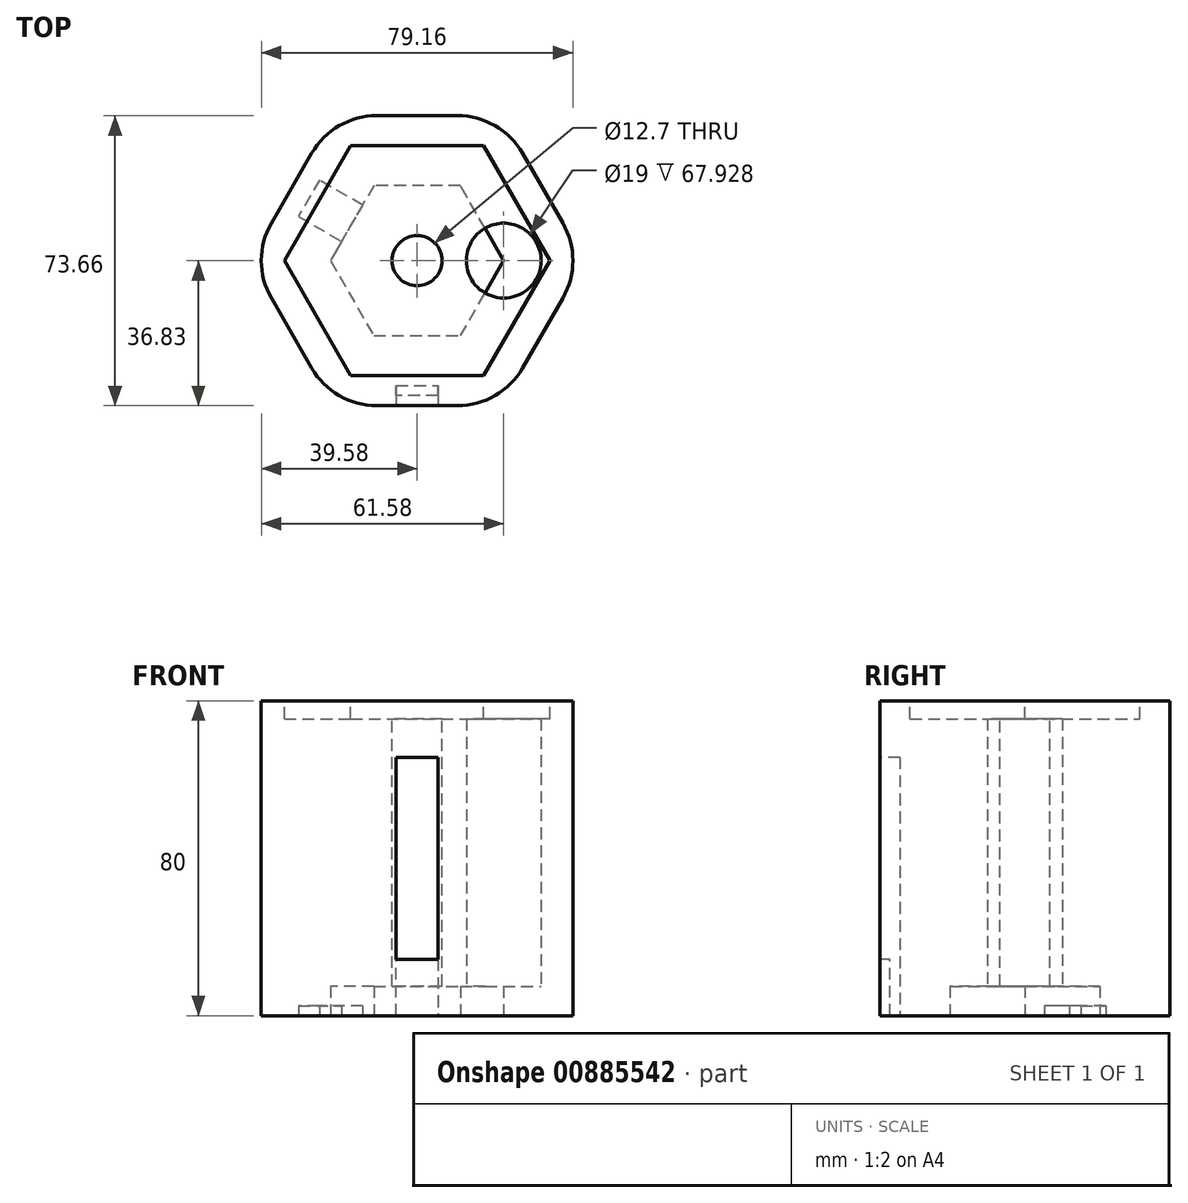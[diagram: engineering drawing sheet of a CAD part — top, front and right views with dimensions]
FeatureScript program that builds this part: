
annotation { "Feature Type Name" : "Feature", "Feature Type Description" : "" }
export const myFeature = defineFeature(function(context is Context, id is Id, definition is map)
    precondition{}
    {
        {
            var Q0;
            Q0=qCreatedBy(makeId("Front.planeOp"),FACE);
            var sketch = newSketch(context, id + "F0", { "sketchPlane" : qUnion([Q0])});
            skLineSegment(sketch, "E0", {"start": v(0, 111.03) * mm, "end": v(0, -71.9) * mm});
            skSolve(sketch);
        }
        {
            var Q0;
            Q0=qCreatedBy(makeId("Top.planeOp"),FACE);
            var sketch = newSketch(context, id + "F1", { "sketchPlane" : qUnion([Q0])});
            skCircle(sketch, "E1.cCircle", {"center": v(0, 0) * mm, "radius": 36.83 * mm, "construction": true});
            skLineSegment(sketch, "E1.0", {"start": v(-21.26, 36.83) * mm, "end": v(21.26, 36.83) * mm});
            skLineSegment(sketch, "E1.1", {"start": v(21.26, 36.83) * mm, "end": v(42.53, 0) * mm});
            skLineSegment(sketch, "E1.2", {"start": v(42.53, 0) * mm, "end": v(21.26, -36.83) * mm});
            skLineSegment(sketch, "E1.3", {"start": v(21.26, -36.83) * mm, "end": v(-21.26, -36.83) * mm});
            skLineSegment(sketch, "E1.4", {"start": v(-21.26, -36.83) * mm, "end": v(-42.53, 0) * mm});
            skLineSegment(sketch, "E1.5", {"start": v(-42.53, 0) * mm, "end": v(-21.26, 36.83) * mm});
            skPoint(sketch, "E1.0.midPoint", {"position": v(0, 36.83) * mm});
            skSolve(sketch);
        }
        {
            var Q0;
            Q0=makeQuery(id+"F1.imprint","IMPRINT",FACE,{"disambiguationData":[TD([[makeQuery(id+"F1.imprint","IMPRINT",EDGE,{"derivedFrom":sQuery(id+"F1.wireOp",EDGE,"E1.0")}),-1.0]])]});
            extrude(context, id + "F2", {"entities" : qUnion([Q0]), "depth" : 80 * mm, "offsetDistance" : 25.4 * mm});
        }
        {
            var Q0;
            Q0=qCreatedBy(makeId("Top.planeOp"),FACE);
            cPlane(context, id + "F3", {"entities" : qUnion([Q0]), "cplaneType" : CPlaneType.OFFSET, "offset" : 7.5 * mm, "width" : 152.4 * mm, "height" : 152.4 * mm});
        }
        {
            var Q0;
            Q0=qCreatedBy(id+"F3.planeOp",FACE);
            var sketch = newSketch(context, id + "F4", { "sketchPlane" : qUnion([Q0])});
            skLineSegment(sketch, "E2", {"start": v(0, 0) * mm, "end": v(22, 0) * mm});
            skCircle(sketch, "E3", {"center": v(22, 0) * mm, "radius": 9.5 * mm});
            skSolve(sketch);
        }
        {
            var Q0;
            Q0 = qSketchRegion(id + "F4", true);
            extrude(context, id + "F5", {"entities" : qUnion([Q0]), "operationType" : NewBodyOperationType.REMOVE, "depth" : 68 * mm, "offsetDistance" : 25.4 * mm});
        }
        {
            var Q0;
            Q0=makeQuery(id+"F2.opExtrude","CAP_FACE",FACE,{"disambiguationData":[OSD([sQuery(id+"F1.wireOp",EDGE,"E1.0"),sQuery(id+"F1.wireOp",EDGE,"E1.1"),sQuery(id+"F1.wireOp",EDGE,"E1.2"),sQuery(id+"F1.wireOp",EDGE,"E1.3"),sQuery(id+"F1.wireOp",EDGE,"E1.4"),sQuery(id+"F1.wireOp",EDGE,"E1.5")])],"isStart":false});
            var sketch = newSketch(context, id + "F6", { "sketchPlane" : qUnion([Q0])});
            skCircle(sketch, "E4.cCircle", {"center": v(0, 0) * mm, "radius": 29.2 * mm, "construction": true});
            skLineSegment(sketch, "E4.0", {"start": v(-16.86, 29.2) * mm, "end": v(16.86, 29.2) * mm});
            skLineSegment(sketch, "E4.1", {"start": v(16.86, 29.2) * mm, "end": v(33.73, 0) * mm});
            skLineSegment(sketch, "E4.2", {"start": v(33.73, 0) * mm, "end": v(16.86, -29.2) * mm});
            skLineSegment(sketch, "E4.3", {"start": v(16.86, -29.2) * mm, "end": v(-16.86, -29.21) * mm});
            skLineSegment(sketch, "E4.4", {"start": v(-16.86, -29.21) * mm, "end": v(-33.73, 0) * mm});
            skLineSegment(sketch, "E4.5", {"start": v(-33.73, 0) * mm, "end": v(-16.86, 29.2) * mm});
            skPoint(sketch, "E4.0.midPoint", {"position": v(0, 29.2) * mm});
            skSolve(sketch);
        }
        {
            var Q0;
            Q0=makeQuery(id+"F6.imprint","IMPRINT",FACE,{"disambiguationData":[TD([[makeQuery(id+"F6.imprint","IMPRINT",EDGE,{"derivedFrom":sQuery(id+"F6.wireOp",EDGE,"E4.0")}),-1.0]])]});
            extrude(context, id + "F7", {"entities" : qUnion([Q0]), "operationType" : NewBodyOperationType.REMOVE, "oppositeDirection" : true, "depth" : 4.57 * mm, "offsetDistance" : 25.4 * mm});
        }
        {
            var Q0;
            Q0=makeQuery(id+"F7.boolean.opBoolean","COPY",FACE,{"derivedFrom":makeQuery(id+"F7.opExtrude","CAP_FACE",FACE,{"disambiguationData":[OSD([sQuery(id+"F6.wireOp",EDGE,"E4.0"),sQuery(id+"F6.wireOp",EDGE,"E4.1"),sQuery(id+"F6.wireOp",EDGE,"E4.2"),sQuery(id+"F6.wireOp",EDGE,"E4.3"),sQuery(id+"F6.wireOp",EDGE,"E4.4"),sQuery(id+"F6.wireOp",EDGE,"E4.5")])],"isStart":false})});
            var sketch = newSketch(context, id + "F8", { "sketchPlane" : qUnion([Q0])});
            skCircle(sketch, "E5", {"center": v(0, 0) * mm, "radius": 6.35 * mm});
            skSolve(sketch);
        }
        {
            var Q0;
            Q0 = qSketchRegion(id + "F8", true);
            var Q1;
            Q1=makeQuery(id+"F2.opExtrude","CAP_FACE",FACE,{"disambiguationData":[OSD([sQuery(id+"F1.wireOp",EDGE,"E1.0"),sQuery(id+"F1.wireOp",EDGE,"E1.1"),sQuery(id+"F1.wireOp",EDGE,"E1.2"),sQuery(id+"F1.wireOp",EDGE,"E1.3"),sQuery(id+"F1.wireOp",EDGE,"E1.4"),sQuery(id+"F1.wireOp",EDGE,"E1.5")])],"isStart":true});
            extrude(context, id + "F9", {"entities" : qUnion([Q0]), "operationType" : NewBodyOperationType.REMOVE, "endBound" : BoundingType.UP_TO_SURFACE, "oppositeDirection" : true, "depth" : 25.4 * mm, "endBoundEntityFace" : qUnion([Q1]), "offsetDistance" : 25.4 * mm});
        }
        {
            var Q0;
            Q0=makeQuery(id+"F2.opExtrude","CAP_FACE",FACE,{"disambiguationData":[OSD([sQuery(id+"F1.wireOp",EDGE,"E1.0"),sQuery(id+"F1.wireOp",EDGE,"E1.1"),sQuery(id+"F1.wireOp",EDGE,"E1.2"),sQuery(id+"F1.wireOp",EDGE,"E1.3"),sQuery(id+"F1.wireOp",EDGE,"E1.4"),sQuery(id+"F1.wireOp",EDGE,"E1.5")])],"isStart":true});
            var sketch = newSketch(context, id + "F10", { "sketchPlane" : qUnion([Q0])});
            skCircle(sketch, "E6.cCircle", {"center": v(0, 0) * mm, "radius": 19.05 * mm, "construction": true});
            skLineSegment(sketch, "E6.0", {"start": v(-11, 19.05) * mm, "end": v(11, 19.05) * mm});
            skLineSegment(sketch, "E6.1", {"start": v(11, 19.05) * mm, "end": v(22, 0) * mm});
            skLineSegment(sketch, "E6.2", {"start": v(22, 0) * mm, "end": v(11, -19.05) * mm});
            skLineSegment(sketch, "E6.3", {"start": v(11, -19.05) * mm, "end": v(-11, -19.05) * mm});
            skLineSegment(sketch, "E6.4", {"start": v(-11, -19.05) * mm, "end": v(-22, 0) * mm});
            skLineSegment(sketch, "E6.5", {"start": v(-22, 0) * mm, "end": v(-11, 19.05) * mm});
            skPoint(sketch, "E6.0.midPoint", {"position": v(0, 19.05) * mm});
            skSolve(sketch);
        }
        {
            var Q0;
            Q0=makeQuery(id+"F10.imprint","IMPRINT",FACE,{"disambiguationData":[TD([[makeQuery(id+"F10.imprint","IMPRINT",EDGE,{"derivedFrom":sQuery(id+"F10.wireOp",EDGE,"E6.0")}),-1.0]])]});
            extrude(context, id + "F11", {"entities" : qUnion([Q0]), "operationType" : NewBodyOperationType.REMOVE, "oppositeDirection" : true, "depth" : 7.5 * mm, "offsetDistance" : 25.4 * mm});
        }
        {
            var Q0;
            Q0=makeQuery(id+"F2.opExtrude","SWEPT_FACE",FACE,{"disambiguationData":[OSD([sQuery(id+"F1.wireOp",EDGE,"E1.3")])]});
            var sketch = newSketch(context, id + "F12", { "sketchPlane" : qUnion([Q0])});
            skLineSegment(sketch, "E7", {"start": v(0, 80) * mm, "end": v(0, 0) * mm});
            skLineSegment(sketch, "E8.bottom", {"start": v(5.33, 65.65) * mm, "end": v(-5.33, 65.65) * mm});
            skLineSegment(sketch, "E8.top", {"start": v(5.33, 14.35) * mm, "end": v(-5.33, 14.35) * mm});
            skLineSegment(sketch, "E8.left", {"start": v(5.33, 65.65) * mm, "end": v(5.33, 14.35) * mm});
            skLineSegment(sketch, "E8.right", {"start": v(-5.33, 65.65) * mm, "end": v(-5.33, 14.35) * mm});
            skPoint(sketch, "E8.middle", {"position": v(0, 40) * mm});
            skSolve(sketch);
        }
        {
            var Q0;
            {var subQ5=sQuery(id+"F12.wireOp",EDGE,"E8.right");Q0=makeQuery(id+"F12.imprint","IMPRINT",FACE,{"disambiguationData":[TD([[makeQuery(id+"F12.imprint","IMPRINT",EDGE,{"derivedFrom":subQ5}),1.0]])]});}
            var Q1;
            {var subQ5=sQuery(id+"F12.wireOp",EDGE,"E8.left");Q1=makeQuery(id+"F12.imprint","IMPRINT",FACE,{"disambiguationData":[TD([[makeQuery(id+"F12.imprint","IMPRINT",EDGE,{"derivedFrom":subQ5}),-1.0]])]});}
            extrude(context, id + "F13", {"entities" : qUnion([Q0, Q1]), "operationType" : NewBodyOperationType.REMOVE, "oppositeDirection" : true, "depth" : 5.08 * mm, "offsetDistance" : 25.4 * mm});
        }
        {
            var Q0;
            Q0=makeQuery(id+"F13.boolean.opBoolean","COPY",FACE,{"derivedFrom":makeQuery(id+"F13.opExtrude","SWEPT_FACE",FACE,{"disambiguationData":[OSD([sQuery(id+"F12.wireOp",EDGE,"E8.top")])]})});
            var sketch = newSketch(context, id + "F14", { "sketchPlane" : qUnion([Q0])});
            skLineSegment(sketch, "E9.bottom", {"start": v(5.33, -31.75) * mm, "end": v(-5.33, -31.75) * mm});
            skLineSegment(sketch, "E9.top", {"start": v(5.33, -34.3) * mm, "end": v(-5.33, -34.3) * mm});
            skLineSegment(sketch, "E9.left", {"start": v(5.33, -31.75) * mm, "end": v(5.33, -34.3) * mm});
            skLineSegment(sketch, "E9.right", {"start": v(-5.33, -31.75) * mm, "end": v(-5.33, -34.3) * mm});
            skSolve(sketch);
        }
        {
            var Q0;
            Q0 = qSketchRegion(id + "F14", true);
            var Q1;
            Q1=makeQuery(id+"F2.opExtrude","CAP_FACE",FACE,{"disambiguationData":[OSD([sQuery(id+"F1.wireOp",EDGE,"E1.0"),sQuery(id+"F1.wireOp",EDGE,"E1.1"),sQuery(id+"F1.wireOp",EDGE,"E1.2"),sQuery(id+"F1.wireOp",EDGE,"E1.3"),sQuery(id+"F1.wireOp",EDGE,"E1.4"),sQuery(id+"F1.wireOp",EDGE,"E1.5")])],"isStart":true});
            extrude(context, id + "F15", {"entities" : qUnion([Q0]), "operationType" : NewBodyOperationType.REMOVE, "endBound" : BoundingType.UP_TO_NEXT, "oppositeDirection" : true, "depth" : 25.4 * mm, "endBoundEntityFace" : qUnion([Q1]), "offsetDistance" : 25.4 * mm});
        }
        {
            var Q0;
            Q0=makeQuery(id+"F2.opExtrude","CAP_FACE",FACE,{"disambiguationData":[OSD([sQuery(id+"F1.wireOp",EDGE,"E1.0"),sQuery(id+"F1.wireOp",EDGE,"E1.1"),sQuery(id+"F1.wireOp",EDGE,"E1.2"),sQuery(id+"F1.wireOp",EDGE,"E1.3"),sQuery(id+"F1.wireOp",EDGE,"E1.4"),sQuery(id+"F1.wireOp",EDGE,"E1.5")])],"isStart":false});
            var Q1;
            Q1=qCreatedBy(makeId("Top.planeOp"),FACE);
            cPlane(context, id + "F16", {"entities" : qUnion([Q0, Q1]), "cplaneType" : CPlaneType.MID_PLANE, "offset" : 25.4 * mm, "width" : 152.4 * mm, "height" : 152.4 * mm});
        }
        {
            var Q0;
            Q0=makeQuery(id+"F2.opExtrude","CAP_FACE",FACE,{"disambiguationData":[OSD([sQuery(id+"F1.wireOp",EDGE,"E1.0"),sQuery(id+"F1.wireOp",EDGE,"E1.1"),sQuery(id+"F1.wireOp",EDGE,"E1.2"),sQuery(id+"F1.wireOp",EDGE,"E1.3"),sQuery(id+"F1.wireOp",EDGE,"E1.4"),sQuery(id+"F1.wireOp",EDGE,"E1.5")])],"isStart":true});
            var sketch = newSketch(context, id + "F17", { "sketchPlane" : qUnion([Q0])});
            skLineSegment(sketch, "E10", {"start": v(-24.83, -20.5) * mm, "end": v(-30.16, -11.26) * mm});
            skLineSegment(sketch, "E11", {"start": v(-30.16, -11.26) * mm, "end": v(-19.16, -4.9) * mm});
            skLineSegment(sketch, "E12", {"start": v(-19.16, -4.9) * mm, "end": v(-13.83, -14.14) * mm});
            skLineSegment(sketch, "E13", {"start": v(-13.83, -14.14) * mm, "end": v(-24.83, -20.5) * mm});
            skSolve(sketch);
        }
        {
            var Q0;
            Q0=makeQuery(id+"F17.imprint","IMPRINT",FACE,{"disambiguationData":[TD([[makeQuery(id+"F17.imprint","IMPRINT",EDGE,{"derivedFrom":sQuery(id+"F17.wireOp",EDGE,"E10")}),-1.0]])]});
            extrude(context, id + "F18", {"entities" : qUnion([Q0]), "operationType" : NewBodyOperationType.REMOVE, "oppositeDirection" : true, "depth" : 2.54 * mm, "offsetDistance" : 25.4 * mm});
        }
        {
            var Q0;
            Q0=makeQuery(id+"F2.opExtrude","SWEPT_EDGE",EDGE,{"disambiguationData":[OSD([sQuery(id+"F1.wireOp",EDGE,"E1.0"),sQuery(id+"F1.wireOp",EDGE,"E1.5")])]});
            var Q1;
            Q1=makeQuery(id+"F2.opExtrude","SWEPT_EDGE",EDGE,{"disambiguationData":[OSD([sQuery(id+"F1.wireOp",EDGE,"E1.0"),sQuery(id+"F1.wireOp",EDGE,"E1.1")])]});
            var Q2;
            Q2=makeQuery(id+"F2.opExtrude","SWEPT_EDGE",EDGE,{"disambiguationData":[OSD([sQuery(id+"F1.wireOp",EDGE,"E1.1"),sQuery(id+"F1.wireOp",EDGE,"E1.2")])]});
            var Q3;
            Q3=makeQuery(id+"F2.opExtrude","SWEPT_EDGE",EDGE,{"disambiguationData":[OSD([sQuery(id+"F1.wireOp",EDGE,"E1.2"),sQuery(id+"F1.wireOp",EDGE,"E1.3")])]});
            var Q4;
            Q4=makeQuery(id+"F2.opExtrude","SWEPT_EDGE",EDGE,{"disambiguationData":[OSD([sQuery(id+"F1.wireOp",EDGE,"E1.3"),sQuery(id+"F1.wireOp",EDGE,"E1.4")])]});
            var Q5;
            Q5=makeQuery(id+"F2.opExtrude","SWEPT_EDGE",EDGE,{"disambiguationData":[OSD([sQuery(id+"F1.wireOp",EDGE,"E1.4"),sQuery(id+"F1.wireOp",EDGE,"E1.5")])]});
            fillet(context, id + "F19", {"entities" : qUnion([Q0, Q1, Q2, Q3, Q4, Q5]), "radius" : 19.05 * mm, "tangentPropagation" : true, "allowEdgeOverflow" : false});
        }
    });
